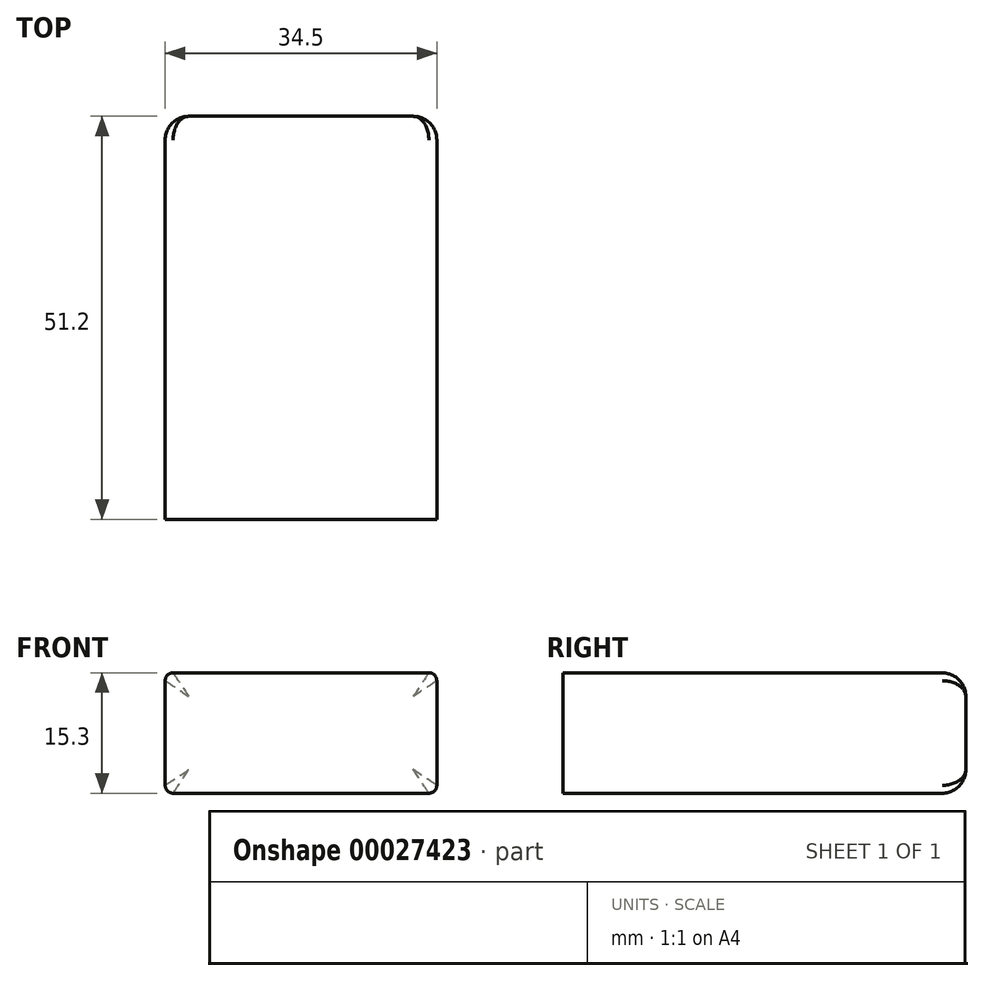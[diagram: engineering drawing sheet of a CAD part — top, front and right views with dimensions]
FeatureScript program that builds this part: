
annotation { "Feature Type Name" : "Feature", "Feature Type Description" : "" }
export const myFeature = defineFeature(function(context is Context, id is Id, definition is map)
    precondition{}
    {
        {
            var Q0;
            Q0=qCreatedBy(makeId("Top.planeOp"),FACE);
            var sketch = newSketch(context, id + "F0", { "sketchPlane" : qUnion([Q0])});
            skLineSegment(sketch, "E0.rect.bottom", {"start": v(17.25, -25.6) * mm, "end": v(-17.25, -25.6) * mm});
            skLineSegment(sketch, "E0.rect.top", {"start": v(17.25, 25.6) * mm, "end": v(-17.25, 25.6) * mm});
            skLineSegment(sketch, "E0.rect.left", {"start": v(17.25, -25.6) * mm, "end": v(17.25, 25.6) * mm});
            skLineSegment(sketch, "E0.rect.right", {"start": v(-17.25, -25.6) * mm, "end": v(-17.25, 25.6) * mm});
            skPoint(sketch, "E0.rect.middle", {"position": v(0, 0) * mm});
            skSolve(sketch);
        }
        {
            var Q0;
            Q0=makeQuery(id+"F0.imprint","IMPRINT",FACE,{"disambiguationData":[TD([[makeQuery(id+"F0.imprint","IMPRINT",EDGE,{"derivedFrom":sQuery(id+"F0.wireOp",EDGE,"E0.rect.bottom")}),-1.0]])]});
            extrude(context, id + "F1", {"entities" : qUnion([Q0]), "depth" : 15.3 * mm});
        }
        {
            var Q0;
            Q0=makeQuery(id+"F1.opExtrude","CAP_EDGE",EDGE,{"disambiguationData":[OSD([sQuery(id+"F0.wireOp",EDGE,"E0.rect.left")])],"isStart":false});
            var Q1;
            Q1=makeQuery(id+"F1.opExtrude","CAP_EDGE",EDGE,{"disambiguationData":[OSD([sQuery(id+"F0.wireOp",EDGE,"E0.rect.left")])],"isStart":true});
            var Q2;
            Q2=makeQuery(id+"F1.opExtrude","CAP_EDGE",EDGE,{"disambiguationData":[OSD([sQuery(id+"F0.wireOp",EDGE,"E0.rect.right")])],"isStart":true});
            var Q3;
            Q3=makeQuery(id+"F1.opExtrude","CAP_EDGE",EDGE,{"disambiguationData":[OSD([sQuery(id+"F0.wireOp",EDGE,"E0.rect.right")])],"isStart":false});
            fillet(context, id + "F2", {"entities" : qUnion([Q0, Q1, Q2, Q3]), "radius" : 1 * mm, "tangentPropagation" : true, "allowEdgeOverflow" : false});
        }
        {
            var Q0;
            Q0=makeQuery(id+"F1.opExtrude","CAP_EDGE",EDGE,{"disambiguationData":[OSD([sQuery(id+"F0.wireOp",EDGE,"E0.rect.top")])],"isStart":false});
            fillet(context, id + "F3", {"entities" : qUnion([Q0]), "radius" : 3 * mm, "tangentPropagation" : true, "allowEdgeOverflow" : false});
        }
    });
